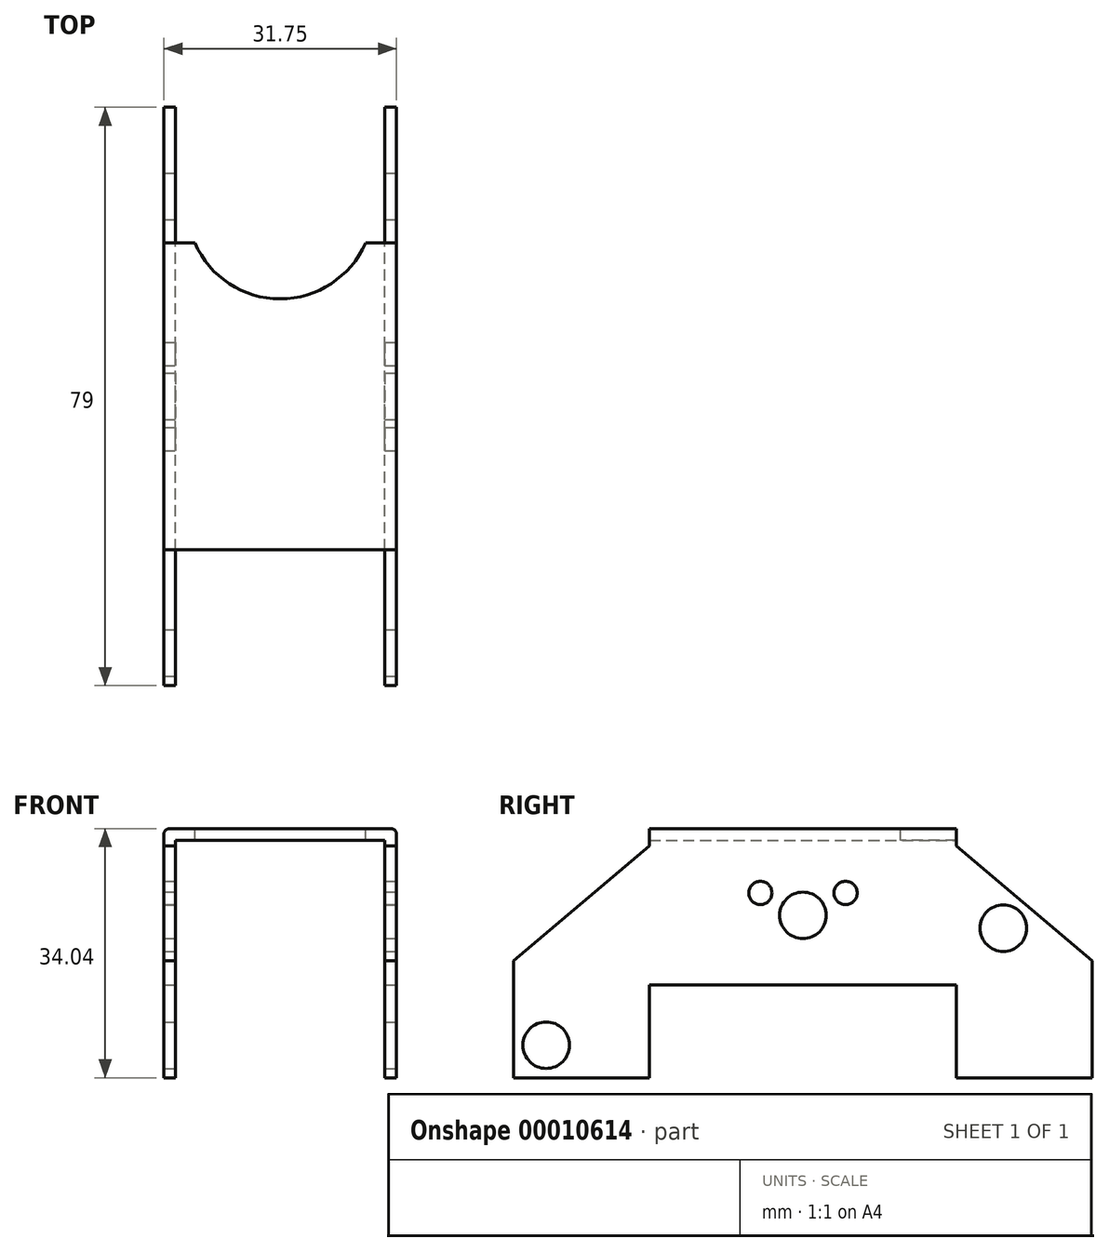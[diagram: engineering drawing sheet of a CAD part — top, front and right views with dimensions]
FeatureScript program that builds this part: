
annotation { "Feature Type Name" : "Feature", "Feature Type Description" : "" }
export const myFeature = defineFeature(function(context is Context, id is Id, definition is map)
    precondition{}
    {
        {
            var Q0;
            Q0=qCreatedBy(makeId("Right.planeOp"),FACE);
            var sketch = newSketch(context, id + "F0", { "sketchPlane" : qUnion([Q0])});
            skLineSegment(sketch, "E0.rect.bottom", {"start": v(39.5, -17.02) * mm, "end": v(20.96, -17.02) * mm});
            skLineSegment(sketch, "E0.rect.top", {"start": v(20.95, 14.63) * mm, "end": v(-20.96, 14.63) * mm});
            skLineSegment(sketch, "E0.rect.left", {"start": v(39.5, -17.02) * mm, "end": v(39.5, -1.02) * mm});
            skLineSegment(sketch, "E0.rect.right", {"start": v(-39.5, -17.02) * mm, "end": v(-39.5, -1.02) * mm});
            skPoint(sketch, "E0.rect.middle", {"position": v(0, 0) * mm});
            skLineSegment(sketch, "E1", {"start": v(-39.5, -4.32) * mm, "end": v(39.5, -4.32) * mm, "construction": true});
            skLineSegment(sketch, "E2", {"start": v(-20.96, 14.63) * mm, "end": v(-20.96, -17.02) * mm, "construction": true});
            skLineSegment(sketch, "E3", {"start": v(20.95, 14.63) * mm, "end": v(20.96, -17.02) * mm, "construction": true});
            skLineSegment(sketch, "E4", {"start": v(-39.5, -1.02) * mm, "end": v(39.5, -1.02) * mm, "construction": true});
            skLineSegment(sketch, "E5", {"start": v(39.5, -1.02) * mm, "end": v(20.95, 14.63) * mm});
            skLineSegment(sketch, "E6", {"start": v(-39.5, -1.02) * mm, "end": v(-20.96, 14.63) * mm});
            skLineSegment(sketch, "E7.trimOffspring", {"start": v(-20.95, -17.02) * mm, "end": v(-39.5, -17.02) * mm});
            skLineSegment(sketch, "E8", {"start": v(-20.96, -17.02) * mm, "end": v(-20.96, -4.32) * mm});
            skLineSegment(sketch, "E9", {"start": v(-20.96, -4.32) * mm, "end": v(20.96, -4.32) * mm});
            skLineSegment(sketch, "E10", {"start": v(20.96, -4.32) * mm, "end": v(20.96, -17.02) * mm});
            skLineSegment(sketch, "E11.bottom", {"start": v(-20.96, 14.63) * mm, "end": v(20.95, 14.63) * mm});
            skLineSegment(sketch, "E11.top", {"start": v(-20.96, 15.42) * mm, "end": v(20.95, 15.42) * mm});
            skLineSegment(sketch, "E11.left", {"start": v(-20.96, 14.63) * mm, "end": v(-20.96, 15.42) * mm});
            skLineSegment(sketch, "E11.right", {"start": v(20.95, 14.63) * mm, "end": v(20.95, 15.42) * mm});
            skLineSegment(sketch, "E12.top", {"start": v(-20.96, 17.02) * mm, "end": v(20.95, 17.02) * mm});
            skLineSegment(sketch, "E12.left", {"start": v(-20.96, 15.42) * mm, "end": v(-20.96, 17.02) * mm});
            skLineSegment(sketch, "E12.right", {"start": v(20.95, 15.42) * mm, "end": v(20.95, 17.02) * mm});
            skCircle(sketch, "E13", {"center": v(0, 5.16) * mm, "radius": 3.18 * mm});
            skCircle(sketch, "E14", {"center": v(-35.05, -12.57) * mm, "radius": 3.18 * mm});
            skCircle(sketch, "E15", {"center": v(5.82, 8.21) * mm, "radius": 1.59 * mm});
            skLineSegment(sketch, "E16", {"start": v(0, 17.02) * mm, "end": v(0, -4.32) * mm, "construction": true});
            skCircle(sketch, "E17.0.MirrorC", {"center": v(-5.82, 8.21) * mm, "radius": 1.59 * mm});
            skLineSegment(sketch, "E18", {"start": v(30.23, 6.8) * mm, "end": v(27.36, 3.41) * mm, "construction": true});
            skCircle(sketch, "E19", {"center": v(27.36, 3.41) * mm, "radius": 3.18 * mm});
            skSolve(sketch);
        }
        {
            var Q0;
            Q0=qSketchRegion(id+"F0",true);
            extrude(context, id + "F1", {"entities" : qUnion([Q0]), "oppositeDirection" : true, "depth" : 1.57 * mm});
        }
        {
            var Q0;
            Q0=qSketchRegion(id+"F0",true);
            extrude(context, id + "F2", {"entities" : qUnion([Q0]), "operationType" : NewBodyOperationType.ADD, "oppositeDirection" : true, "depth" : 1.6 * mm});
        }
        {
            var Q0;
            Q0=makeQuery(id+"F2.opExtrude","CAP_FACE",FACE,{"disambiguationData":[OSD([sQuery(id+"F0.wireOp",EDGE,"E0.rect.bottom"),sQuery(id+"F0.wireOp",EDGE,"E0.rect.left"),sQuery(id+"F0.wireOp",EDGE,"E0.rect.right"),sQuery(id+"F0.wireOp",EDGE,"E5"),sQuery(id+"F0.wireOp",EDGE,"E6"),sQuery(id+"F0.wireOp",EDGE,"E7.trimOffspring"),sQuery(id+"F0.wireOp",EDGE,"E8"),sQuery(id+"F0.wireOp",EDGE,"E9"),sQuery(id+"F0.wireOp",EDGE,"E10"),sQuery(id+"F0.wireOp",EDGE,"E11.left"),sQuery(id+"F0.wireOp",EDGE,"E11.right"),sQuery(id+"F0.wireOp",EDGE,"E12.top"),sQuery(id+"F0.wireOp",EDGE,"E12.left"),sQuery(id+"F0.wireOp",EDGE,"E12.right")])],"isStart":false});
            var sketch = newSketch(context, id + "F3", { "sketchPlane" : qUnion([Q0])});
            skLineSegment(sketch, "E20.0", {"start": v(20.96, 17.02) * mm, "end": v(-20.95, 17.02) * mm});
            skLineSegment(sketch, "E21.0", {"start": v(20.96, 15.42) * mm, "end": v(-20.95, 15.42) * mm});
            skLineSegment(sketch, "E22.0", {"start": v(-20.95, 15.42) * mm, "end": v(-20.95, 17.02) * mm});
            skLineSegment(sketch, "E23.0", {"start": v(20.96, 15.42) * mm, "end": v(20.96, 17.02) * mm});
            skSolve(sketch);
        }
        {
            var Q0;
            Q0=qSketchRegion(id+"F3",true);
            extrude(context, id + "F4", {"entities" : qUnion([Q0]), "operationType" : NewBodyOperationType.ADD, "depth" : 28.57 * mm});
        }
        {
            var Q0;
            Q0=makeQuery(id+"F4.opExtrude","CAP_FACE",FACE,{"disambiguationData":[OSD([sQuery(id+"F3.wireOp",EDGE,"E20.0"),sQuery(id+"F3.wireOp",EDGE,"E21.0"),sQuery(id+"F3.wireOp",EDGE,"E22.0"),sQuery(id+"F3.wireOp",EDGE,"E23.0")])],"isStart":false});
            var sketch = newSketch(context, id + "F5", { "sketchPlane" : qUnion([Q0])});
            skLineSegment(sketch, "E24.0", {"start": v(20.96, -4.32) * mm, "end": v(-20.96, -4.32) * mm});
            skLineSegment(sketch, "E25.0", {"start": v(20.96, -17.02) * mm, "end": v(20.96, -4.32) * mm});
            skLineSegment(sketch, "E26.0", {"start": v(20.95, -17.02) * mm, "end": v(39.5, -17.02) * mm});
            skLineSegment(sketch, "E27.0", {"start": v(39.5, -17.02) * mm, "end": v(39.5, -1.02) * mm});
            skLineSegment(sketch, "E28.0", {"start": v(39.5, -1.02) * mm, "end": v(20.96, 14.63) * mm});
            skLineSegment(sketch, "E29.0", {"start": v(20.96, 14.63) * mm, "end": v(20.96, 15.42) * mm});
            skLineSegment(sketch, "E30.0", {"start": v(20.96, 15.42) * mm, "end": v(20.96, 17.02) * mm});
            skLineSegment(sketch, "E31.0", {"start": v(20.96, 17.02) * mm, "end": v(-20.95, 17.02) * mm});
            skLineSegment(sketch, "E32.0", {"start": v(-20.95, 15.42) * mm, "end": v(-20.95, 17.02) * mm});
            skLineSegment(sketch, "E33.0", {"start": v(-20.95, 14.63) * mm, "end": v(-20.95, 15.42) * mm});
            skLineSegment(sketch, "E34.0", {"start": v(-39.5, -1.02) * mm, "end": v(-20.95, 14.63) * mm});
            skLineSegment(sketch, "E35.0", {"start": v(-39.5, -17.02) * mm, "end": v(-39.5, -1.02) * mm});
            skLineSegment(sketch, "E36.0", {"start": v(-39.5, -17.02) * mm, "end": v(-20.96, -17.02) * mm});
            skLineSegment(sketch, "E37.0", {"start": v(-20.96, -4.32) * mm, "end": v(-20.96, -17.02) * mm});
            skCircle(sketch, "E38.0", {"center": v(-5.82, 8.21) * mm, "radius": 1.59 * mm});
            skCircle(sketch, "E39.0", {"center": v(0, 5.16) * mm, "radius": 3.18 * mm});
            skCircle(sketch, "E40.0", {"center": v(5.82, 8.21) * mm, "radius": 1.59 * mm});
            skCircle(sketch, "E41.0", {"center": v(35.05, -12.57) * mm, "radius": 3.18 * mm});
            skLineSegment(sketch, "E42.0", {"start": v(0, 17.02) * mm, "end": v(0, -4.32) * mm, "construction": true});
            skCircle(sketch, "E43.0", {"center": v(-27.36, 3.41) * mm, "radius": 3.18 * mm});
            skSolve(sketch);
        }
        {
            var Q0;
            Q0=qSketchRegion(id+"F5",true);
            extrude(context, id + "F6", {"entities" : qUnion([Q0]), "operationType" : NewBodyOperationType.ADD, "depth" : 1.57 * mm});
        }
        {
            var Q0;
            Q0=makeQuery(id+"F4.opExtrude","CAP_EDGE",EDGE,{"disambiguationData":[OSD([sQuery(id+"F3.wireOp",EDGE,"E21.0")])],"isStart":true});
            var Q1;
            Q1=makeQuery(id+"F4.opExtrude","CAP_EDGE",EDGE,{"disambiguationData":[OSD([sQuery(id+"F3.wireOp",EDGE,"E21.0")])],"isStart":false});
            var Q2;
            Q2=makeQuery(id+"F6.opExtrude","CAP_EDGE",EDGE,{"disambiguationData":[OSD([sQuery(id+"F5.wireOp",EDGE,"E31.0")])],"isStart":false});
            var Q3;
            Q3=makeQuery(id+"F1.opExtrude","CAP_EDGE",EDGE,{"disambiguationData":[OSD([sQuery(id+"F0.wireOp",EDGE,"E12.top")])],"isStart":true});
            fillet(context, id + "F7", {"entities" : qUnion([Q0, Q1, Q2, Q3]), "radius" : 0.79 * mm, "tangentPropagation" : true, "allowEdgeOverflow" : false});
        }
        {
            var Q0;
            {var subQ0=sQuery(id+"F0.wireOp",EDGE,"E12.top");Q0=makeQuery(id+"F6.boolean.opBoolean","MERGE",FACE,{"derivedFrom":[makeQuery(id+"F4.boolean.opBoolean","MERGE",FACE,{"derivedFrom":[makeQuery(id+"F2.boolean.opBoolean","MERGE",FACE,{"derivedFrom":[makeQuery(id+"F1.opExtrude","SWEPT_FACE",FACE,{"disambiguationData":[OSD([subQ0])]}),makeQuery(id+"F2.opExtrude","SWEPT_FACE",FACE,{"disambiguationData":[OSD([subQ0])]})]}),makeQuery(id+"F4.opExtrude","SWEPT_FACE",FACE,{"disambiguationData":[OSD([sQuery(id+"F3.wireOp",EDGE,"E20.0")])]})]}),makeQuery(id+"F6.opExtrude","SWEPT_FACE",FACE,{"disambiguationData":[OSD([sQuery(id+"F5.wireOp",EDGE,"E31.0")])]})]});}
            var sketch = newSketch(context, id + "F8", { "sketchPlane" : qUnion([Q0])});
            skLineSegment(sketch, "E44.0", {"start": v(0, -20.96) * mm, "end": v(0, 20.95) * mm, "construction": true});
            skLineSegment(sketch, "E45.0", {"start": v(-30.96, -20.96) * mm, "end": v(-0.79, -20.96) * mm, "construction": true});
            skLineSegment(sketch, "E46", {"start": v(-15.88, -20.96) * mm, "end": v(-15.88, 42.98) * mm, "construction": true});
            skArc(sketch, "E47", {"start": v(-27.51, 20.95) * mm, "mid": v(-15.88, 13.33) * mm, "end": v(-4.24, 20.95) * mm});
            skLineSegment(sketch, "E48.0", {"start": v(-30.96, 20.95) * mm, "end": v(-0.79, 20.95) * mm, "construction": true});
            skLineSegment(sketch, "E49", {"start": v(-4.24, 20.95) * mm, "end": v(-27.51, 20.95) * mm});
            skSolve(sketch);
        }
        {
            var Q0;
            Q0=qSketchRegion(id+"F8",true);
            extrude(context, id + "F9", {"entities" : qUnion([Q0]), "operationType" : NewBodyOperationType.REMOVE, "endBound" : BoundingType.UP_TO_NEXT, "oppositeDirection" : true, "depth" : 5.08 * mm});
        }
    });
